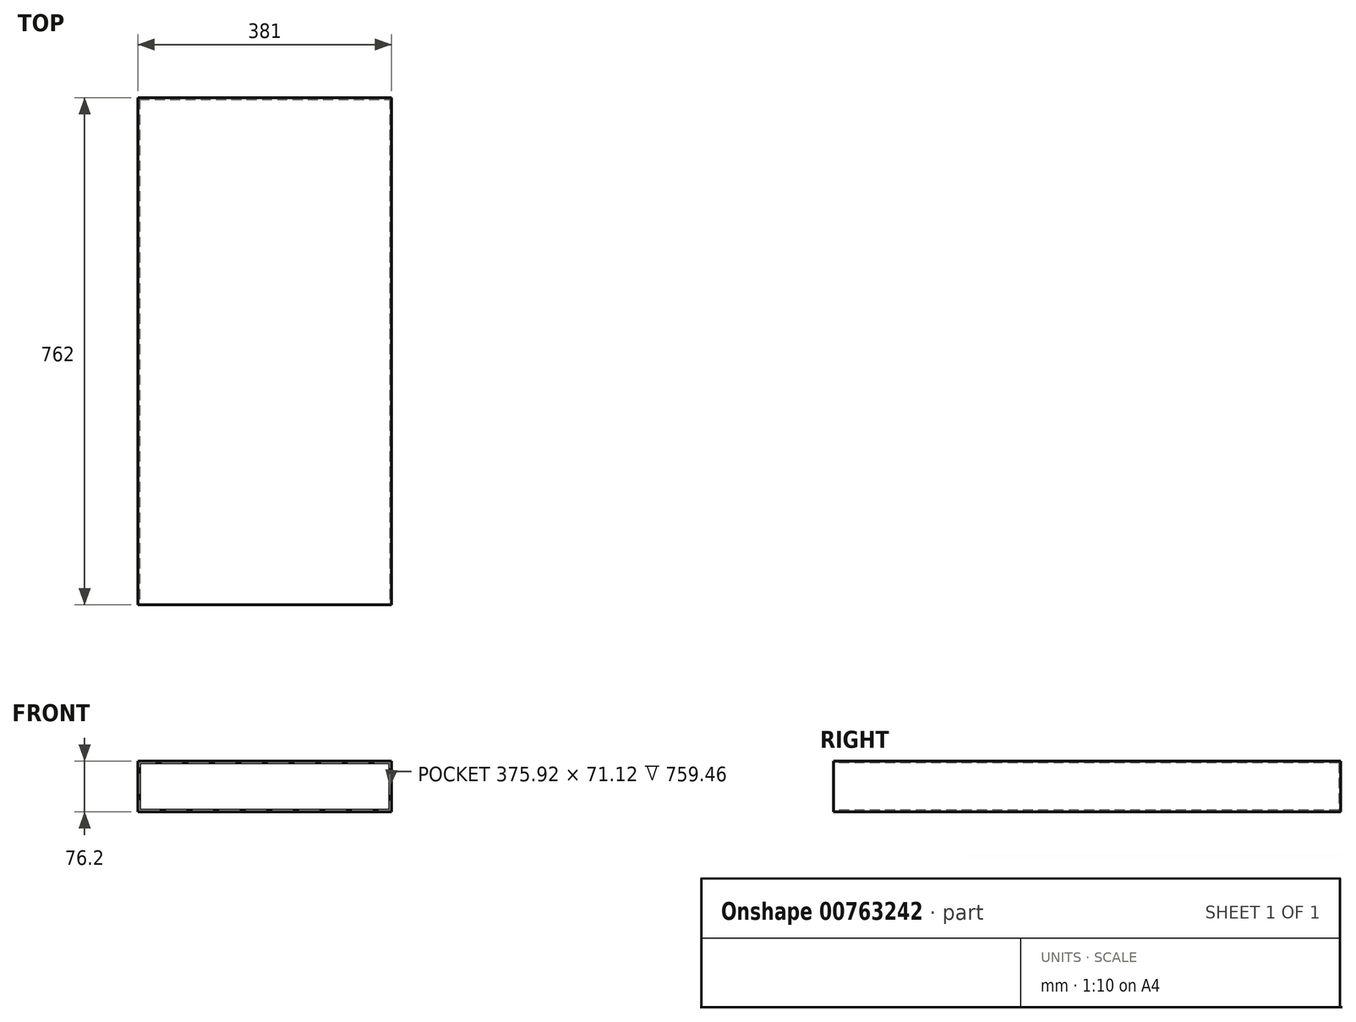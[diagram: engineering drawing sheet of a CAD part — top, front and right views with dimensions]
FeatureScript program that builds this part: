
annotation { "Feature Type Name" : "Feature", "Feature Type Description" : "" }
export const myFeature = defineFeature(function(context is Context, id is Id, definition is map)
    precondition{}
    {
        {
            var Q0;
            Q0=qCreatedBy(makeId("Front.planeOp"),FACE);
            var sketch = newSketch(context, id + "F0", { "sketchPlane" : qUnion([Q0])});
            skLineSegment(sketch, "E0.bottom", {"start": v(-190.5, 38.1) * mm, "end": v(190.5, 38.1) * mm});
            skLineSegment(sketch, "E0.top", {"start": v(-190.5, -38.1) * mm, "end": v(190.5, -38.1) * mm});
            skLineSegment(sketch, "E0.left", {"start": v(-190.5, 38.1) * mm, "end": v(-190.5, -38.1) * mm});
            skLineSegment(sketch, "E0.right", {"start": v(190.5, 38.1) * mm, "end": v(190.5, -38.1) * mm});
            skPoint(sketch, "E0.middle", {"position": v(0, 0) * mm});
            skSolve(sketch);
        }
        {
            var Q0;
            Q0=makeQuery(id+"F0.imprint","IMPRINT",FACE,{"disambiguationData":[TD([[makeQuery(id+"F0.imprint","IMPRINT",EDGE,{"derivedFrom":sQuery(id+"F0.wireOp",EDGE,"E0.bottom")}),-1.0]])]});
            extrude(context, id + "F1", {"entities" : qUnion([Q0]), "oppositeDirection" : true, "depth" : 762 * mm, "offsetDistance" : 25.4 * mm});
        }
        {
            var Q0;
            Q0=makeQuery(id+"F1.opExtrude","CAP_FACE",FACE,{"disambiguationData":[OSD([sQuery(id+"F0.wireOp",EDGE,"E0.bottom"),sQuery(id+"F0.wireOp",EDGE,"E0.top"),sQuery(id+"F0.wireOp",EDGE,"E0.left"),sQuery(id+"F0.wireOp",EDGE,"E0.right")])],"isStart":true});
            shell(context, id + "F2", {"entities" : qUnion([Q0]), "thickness" : 2.54 * mm});
        }
    });
